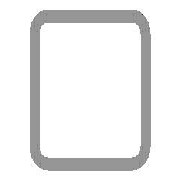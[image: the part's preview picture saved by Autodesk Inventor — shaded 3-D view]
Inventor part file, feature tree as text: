
AUTODESK INVENTOR PART (.ipt)
format: ipt  version: 2025 (Build 290162010, 162A)  size: 137,728 bytes
history: native  units: mm (DEFAULTED — no unit token found)
features: other x4, plane x2, split x1, sketch x1
ambient origin geometry x8: Origin, YZ Plane, XZ Plane, XY Plane, X Axis, Y Axis, Z Axis, Center Point
bodies: Solid1 (feature_tree), Body (feature_tree)
feature tree (8):
  parser-record x1  (decoder bookkeeping rows leaked as tree rows — omitted from the tree; the rows remain in map.json)
  other  "Driven Length"
  other  "Start Plane"
  other  "End Plane"
  plane  "Work Plane4"
  split  "Split1"
  sketch  "Sketch3"  dims[d3=3140.0mm d4=0.0mm d7=8.0mm d9=60.0mm d11=60.0mm d12=4.0mm d13=60.0mm d14=3200.0mm d15=30.0mm d16=30.0mm d17=90.0deg d18=3140.0mm]
  plane  "Work Plane3"
